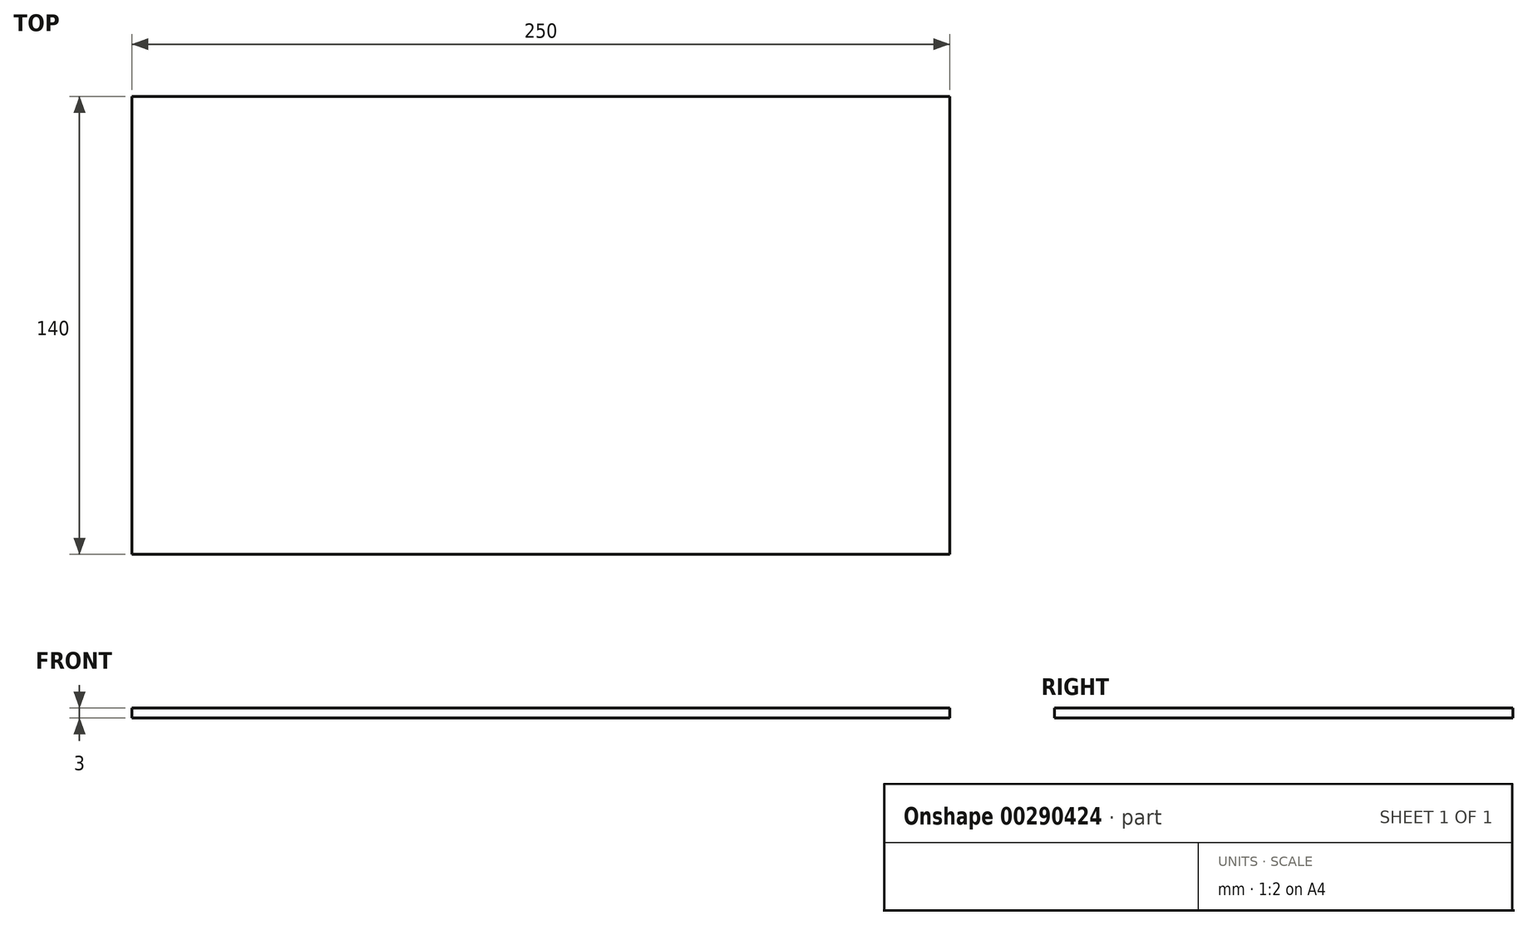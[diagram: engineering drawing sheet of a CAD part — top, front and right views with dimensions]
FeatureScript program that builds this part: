
annotation { "Feature Type Name" : "Feature", "Feature Type Description" : "" }
export const myFeature = defineFeature(function(context is Context, id is Id, definition is map)
    precondition{}
    {
        {
            var Q0;
            Q0=qCreatedBy(makeId("Top.planeOp"),FACE);
            var sketch = newSketch(context, id + "F0", { "sketchPlane" : qUnion([Q0])});
            skLineSegment(sketch, "E0.bottom", {"start": v(-125, -70) * mm, "end": v(125, -70) * mm});
            skLineSegment(sketch, "E0.top", {"start": v(-125, 70) * mm, "end": v(125, 70) * mm});
            skLineSegment(sketch, "E0.left", {"start": v(-125, -70) * mm, "end": v(-125, 70) * mm});
            skLineSegment(sketch, "E0.right", {"start": v(125, -70) * mm, "end": v(125, 70) * mm});
            skPoint(sketch, "E0.middle", {"position": v(0, 0) * mm});
            skSolve(sketch);
        }
        {
            var Q0;
            Q0 = qSketchRegion(id + "F0", true);
            extrude(context, id + "F1", {"entities" : qUnion([Q0]), "depth" : 3 * mm, "offsetDistance" : 25 * mm});
        }
    });
